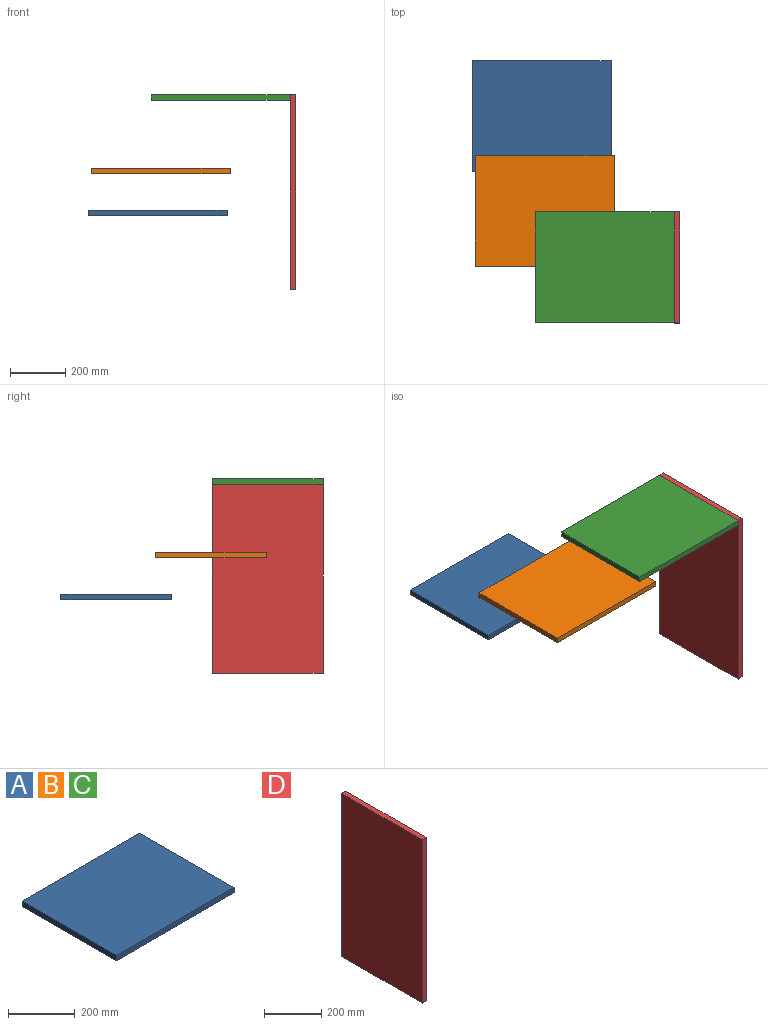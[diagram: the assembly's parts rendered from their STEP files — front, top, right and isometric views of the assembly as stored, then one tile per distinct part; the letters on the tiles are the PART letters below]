
ASSEMBLY  parts=4 mates=1
PART A: 6 faces, bbox 500x400x20 mm
  f0: plane 500x20mm, normal (0,-1,0), area 10000mm2, adj f1,f3,f4,f5
  f1: plane 400x20mm, normal (1,0,0), area 8000mm2, adj f0,f2,f4,f5
  f2: plane 500x20mm, normal (0,1,0), area 10000mm2, adj f1,f3,f4,f5
  f3: plane 400x20mm, normal (-1,0,0), area 8000mm2, adj f0,f2,f4,f5
  f4: plane 500x400mm, normal (0,0,1), area 200000mm2, adj f0,f1,f2,f3
  f5: plane 500x400mm, normal (0,0,-1), area 200000mm2, adj f0,f1,f2,f3
PART B: same geometry as A
PART C: same geometry as A
PART D: 6 faces, bbox 20x400x700 mm
  f0: plane 400x20mm, normal (0,0,-1), area 8000mm2, adj f1,f3,f4,f5
  f1: plane 700x20mm, normal (0,1,0), area 14000mm2, adj f0,f2,f4,f5
  f2: plane 400x20mm, normal (0,0,1), area 8000mm2, adj f1,f3,f4,f5
  f3: plane 700x20mm, normal (0,-1,0), area 14000mm2, adj f0,f2,f4,f5
  f4: plane 700x400mm, normal (1,0,0), area 280000mm2, adj f0,f1,f2,f3
  f5: plane 700x400mm, normal (-1,0,0), area 280000mm2, adj f0,f1,f2,f3
PLACE A t=(45.48,236.42,6.87)mm
PLACE B t=(56.64,-104.07,159.04)mm
PLACE C t=(272.79,-308.49,422.89)mm
PLACE D t=(522.79,-308.49,92.89)mm
MATE fastened C.f1 <-> D.f5  axis (1,0,0) through (522.79,-508.49,442.89)mm
